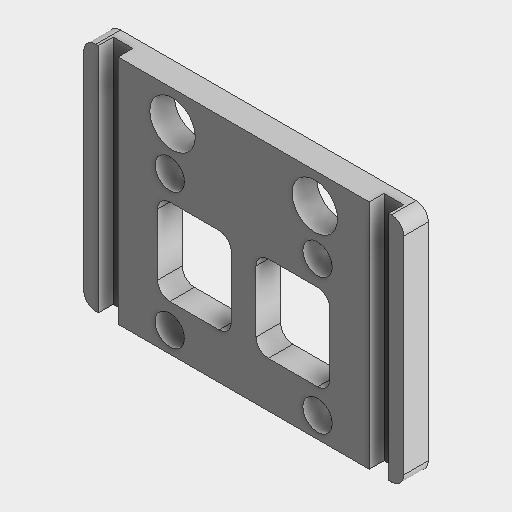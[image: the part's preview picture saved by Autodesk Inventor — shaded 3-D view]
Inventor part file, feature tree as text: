
AUTODESK INVENTOR PART (.ipt)
format: ipt  version: 2019 (Build 230136000, 136)  size: 232,960 bytes
history: native  units: mm
features: extrude x5, sketch x2, fillet x2, mirror x1
ambient origin geometry x8: Origin, YZ Plane, XZ Plane, XY Plane, X Axis, Y Axis, Z Axis, Center Point
bodies: Solid1 (feature_tree)
feature tree (10):
  sketch  "Sketch1"  dims[d2=12.0mm d3=60.0mm]
  extrude  "Extrusion1"  Depth=60.0mm
  extrude  "Extrusion3"  Depth=10.0mm
  sketch  "Sketch2"  dims[d4=55.0mm d5=10.0mm d6=25.0mm d7=10.0mm d8=17.0mm d9=11.0mm d10=15.0mm d12=18.0mm d13=18.5mm d14=90.0mm d15=72.0mm d16=10.0mm d17=0.0mm d18=30.0mm d21=10.0mm d22=0.0mm d25=10.0mm d26=10.0mm d27=180.0mm d28=22.0mm d30=10.0mm d31=0.0mm d32=10.0mm d33=0.0mm d34=5.0mm d35=57.8mm d36=20.0mm d37=8.0mm d38=6.0mm d39=0.0mm d40=5.0mm]
  extrude  "Extrusion4"  Depth=5.0mm
  extrude  "Extrusion5"  Depth=10.0mm
  mirror  "Mirror2"
  fillet  "Fillet4"  Radius=17.0mm
  extrude  "Extrusion6"  Depth=5.0mm
  fillet  "Fillet5"  Radius=15.0mm
